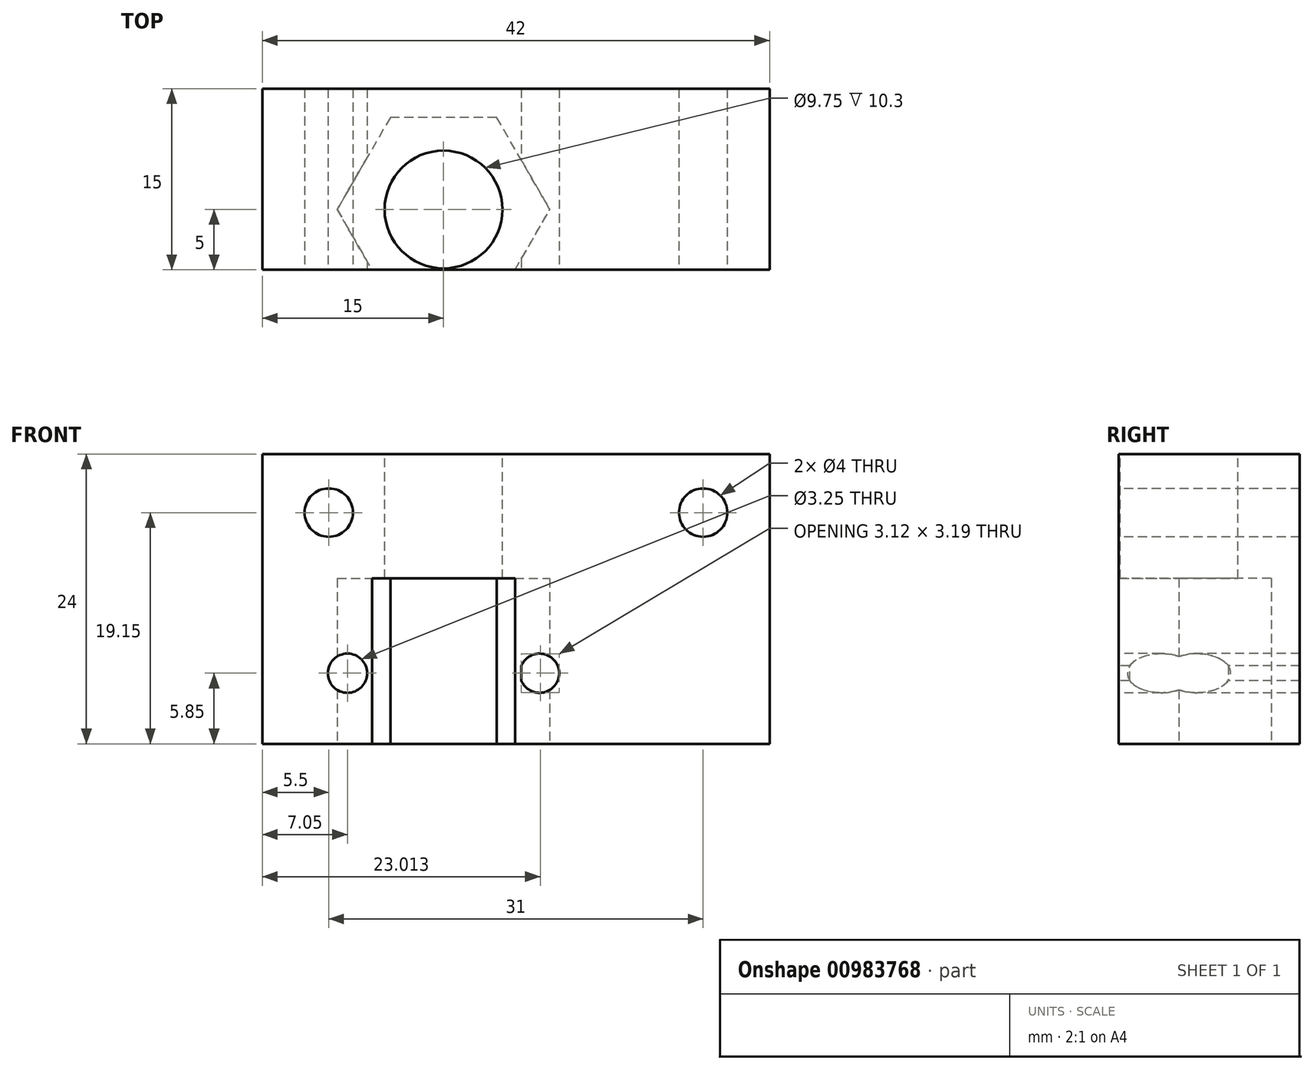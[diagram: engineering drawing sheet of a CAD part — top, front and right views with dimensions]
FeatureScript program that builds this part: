
annotation { "Feature Type Name" : "Feature", "Feature Type Description" : "" }
export const myFeature = defineFeature(function(context is Context, id is Id, definition is map)
    precondition{}
    {
        {
            var Q0;
            Q0=qCreatedBy(makeId("Front.planeOp"),FACE);
            var sketch = newSketch(context, id + "F0", { "sketchPlane" : qUnion([Q0])});
            skLineSegment(sketch, "E0.bottom", {"start": v(0, 0) * mm, "end": v(42, 0) * mm});
            skLineSegment(sketch, "E0.top", {"start": v(0, 24) * mm, "end": v(42, 24) * mm});
            skLineSegment(sketch, "E0.left", {"start": v(0, 0) * mm, "end": v(0, 24) * mm});
            skLineSegment(sketch, "E0.right", {"start": v(42, 0) * mm, "end": v(42, 24) * mm});
            skSolve(sketch);
        }
        {
            var Q0;
            Q0=makeQuery(id+"F0.imprint","IMPRINT",FACE,{"disambiguationData":[TD([[makeQuery(id+"F0.imprint","IMPRINT",EDGE,{"derivedFrom":sQuery(id+"F0.wireOp",EDGE,"E0.bottom")}),1.0]])]});
            extrude(context, id + "F1", {"entities" : qUnion([Q0]), "depth" : 15 * mm, "offsetDistance" : 25 * mm});
        }
        {
            var Q0;
            Q0=makeQuery(id+"F1.opExtrude","CAP_FACE",FACE,{"disambiguationData":[OSD([sQuery(id+"F0.wireOp",EDGE,"E0.bottom"),sQuery(id+"F0.wireOp",EDGE,"E0.top"),sQuery(id+"F0.wireOp",EDGE,"E0.left"),sQuery(id+"F0.wireOp",EDGE,"E0.right")])],"isStart":false});
            var sketch = newSketch(context, id + "F2", { "sketchPlane" : qUnion([Q0])});
            skCircle(sketch, "E1", {"center": v(5.5, 19.15) * mm, "radius": 2 * mm});
            skCircle(sketch, "E2", {"center": v(36.5, 19.15) * mm, "radius": 2 * mm});
            skSolve(sketch);
        }
        {
            var Q0;
            Q0=makeQuery(id+"F2.imprint","IMPRINT",FACE,{"disambiguationData":[TD([[makeQuery(id+"F2.imprint","IMPRINT",EDGE,{"derivedFrom":sQuery(id+"F2.wireOp",EDGE,"E1")}),1.0]])]});
            var Q1;
            Q1=makeQuery(id+"F2.imprint","IMPRINT",FACE,{"disambiguationData":[TD([[makeQuery(id+"F2.imprint","IMPRINT",EDGE,{"derivedFrom":sQuery(id+"F2.wireOp",EDGE,"E2")}),1.0]])]});
            extrude(context, id + "F3", {"entities" : qUnion([Q0, Q1]), "operationType" : NewBodyOperationType.REMOVE, "oppositeDirection" : true, "depth" : 25 * mm, "offsetDistance" : 25 * mm});
        }
        {
            var Q0;
            Q0=makeQuery(id+"F1.opExtrude","SWEPT_FACE",FACE,{"disambiguationData":[OSD([sQuery(id+"F0.wireOp",EDGE,"E0.top")])]});
            var sketch = newSketch(context, id + "F4", { "sketchPlane" : qUnion([Q0])});
            skCircle(sketch, "E3", {"center": v(15, -10) * mm, "radius": 4.88 * mm});
            skSolve(sketch);
        }
        {
            var Q0;
            Q0=makeQuery(id+"F4.imprint","IMPRINT",FACE,{"disambiguationData":[TD([[makeQuery(id+"F4.imprint","IMPRINT",EDGE,{"derivedFrom":sQuery(id+"F4.wireOp",EDGE,"E3")}),1.0]])]});
            extrude(context, id + "F5", {"entities" : qUnion([Q0]), "operationType" : NewBodyOperationType.REMOVE, "oppositeDirection" : true, "depth" : 10.3 * mm, "offsetDistance" : 25 * mm});
        }
        {
            var Q0;
            Q0=makeQuery(id+"F1.opExtrude","SWEPT_FACE",FACE,{"disambiguationData":[OSD([sQuery(id+"F0.wireOp",EDGE,"E0.bottom")])]});
            var sketch = newSketch(context, id + "F6", { "sketchPlane" : qUnion([Q0])});
            skCircle(sketch, "E4.0", {"center": v(15, 10) * mm, "radius": 4.88 * mm});
            skCircle(sketch, "E5.cCircle", {"center": v(15, 10) * mm, "radius": 7.63 * mm, "construction": true});
            skLineSegment(sketch, "E5.0", {"start": v(10.6, 17.62) * mm, "end": v(19.4, 17.62) * mm});
            skLineSegment(sketch, "E5.1", {"start": v(19.4, 17.63) * mm, "end": v(23.8, 10) * mm});
            skLineSegment(sketch, "E5.2", {"start": v(23.8, 10) * mm, "end": v(19.4, 2.37) * mm});
            skLineSegment(sketch, "E5.3", {"start": v(19.4, 2.38) * mm, "end": v(10.6, 2.38) * mm});
            skLineSegment(sketch, "E5.4", {"start": v(10.6, 2.37) * mm, "end": v(6.2, 10) * mm});
            skLineSegment(sketch, "E5.5", {"start": v(6.2, 10) * mm, "end": v(10.6, 17.63) * mm});
            skPoint(sketch, "E5.0.midPoint", {"position": v(15, 17.62) * mm});
            skSolve(sketch);
        }
        {
            var Q0;
            Q0=makeQuery(id+"F6.imprint","IMPRINT",FACE,{"disambiguationData":[TD([[makeQuery(id+"F6.imprint","IMPRINT",EDGE,{"derivedFrom":sQuery(id+"F6.wireOp",EDGE,"E4.0")}),1.0]])]});
            var Q1;
            Q1=makeQuery(id+"F6.imprint","IMPRINT",FACE,{"disambiguationData":[TD([[makeQuery(id+"F6.imprint","IMPRINT",EDGE,{"derivedFrom":sQuery(id+"F6.wireOp",EDGE,"E4.0")}),-1.0]])]});
            var Q2;
            Q2=makeQuery(id+"F5.boolean.opBoolean","COPY",FACE,{"derivedFrom":makeQuery(id+"F5.opExtrude","CAP_FACE",FACE,{"disambiguationData":[OSD([sQuery(id+"F4.wireOp",EDGE,"E3")])],"isStart":false})});
            extrude(context, id + "F7", {"entities" : qUnion([Q0, Q1]), "operationType" : NewBodyOperationType.REMOVE, "endBound" : BoundingType.UP_TO_SURFACE, "oppositeDirection" : true, "depth" : 25 * mm, "endBoundEntityFace" : qUnion([Q2]), "offsetDistance" : 25 * mm});
        }
        {
            var Q0;
            Q0=makeQuery(id+"F1.opExtrude","CAP_FACE",FACE,{"disambiguationData":[OSD([sQuery(id+"F0.wireOp",EDGE,"E0.bottom"),sQuery(id+"F0.wireOp",EDGE,"E0.top"),sQuery(id+"F0.wireOp",EDGE,"E0.left"),sQuery(id+"F0.wireOp",EDGE,"E0.right")])],"isStart":false});
            var sketch = newSketch(context, id + "F8", { "sketchPlane" : qUnion([Q0])});
            skLineSegment(sketch, "E6.0", {"start": v(23.8, 13.7) * mm, "end": v(23.8, 0) * mm});
            skLineSegment(sketch, "E7.0", {"start": v(6.2, 13.7) * mm, "end": v(6.2, 0) * mm});
            skLineSegment(sketch, "E8.0", {"start": v(10.6, 13.7) * mm, "end": v(19.4, 13.7) * mm});
            skCircle(sketch, "E9", {"center": v(7.05, 5.85) * mm, "radius": 1.63 * mm});
            skCircle(sketch, "E10", {"center": v(22.95, 5.85) * mm, "radius": 1.63 * mm});
            skLineSegment(sketch, "E11", {"start": v(6.2, 7.35) * mm, "end": v(23.8, 7.35) * mm});
            skLineSegment(sketch, "E12", {"start": v(8.55, 0) * mm, "end": v(8.55, 7.35) * mm});
            skLineSegment(sketch, "E13", {"start": v(21.45, 7.35) * mm, "end": v(21.45, 0) * mm});
            skSolve(sketch);
        }
        {
            var Q0;
            {var subQ0=sQuery(id+"F8.wireOp",EDGE,"E9");var subQ1=sQuery(id+"F8.wireOp",EDGE,"E7.0");var subQ2=makeQuery(id+"F8.imprint","INTERSECT",VERTEX,{"disambiguationData":[OD(0.0)],"derivedFrom":[subQ1,subQ0]});Q0=makeQuery(id+"F8.imprint","IMPRINT",FACE,{"disambiguationData":[TD([[makeQuery(id+"F8.imprint","IMPRINT",EDGE,{"disambiguationData":[TD([[subQ2,-1.0]])],"derivedFrom":subQ1}),-1.0]])]});}
            var Q1;
            {var subQ0=sQuery(id+"F8.wireOp",EDGE,"E9");var subQ1=sQuery(id+"F8.wireOp",EDGE,"E7.0");var subQ5=makeQuery(id+"F8.imprint","INTERSECT",VERTEX,{"disambiguationData":[OD(0.0)],"derivedFrom":[subQ1,subQ0]});Q1=makeQuery(id+"F8.imprint","IMPRINT",FACE,{"disambiguationData":[TD([[makeQuery(id+"F8.imprint","IMPRINT",EDGE,{"disambiguationData":[TD([[subQ5,-1.0]])],"derivedFrom":subQ1}),1.0]])]});}
            var Q2;
            {var subQ0=sQuery(id+"F8.wireOp",EDGE,"E11");var subQ1=sQuery(id+"F8.wireOp",EDGE,"E9");var subQ2=makeQuery(id+"F8.imprint","INTERSECT",VERTEX,{"disambiguationData":[OD(0.0)],"derivedFrom":[subQ1,subQ0]});Q2=makeQuery(id+"F8.imprint","IMPRINT",FACE,{"disambiguationData":[TD([[makeQuery(id+"F8.imprint","IMPRINT",EDGE,{"disambiguationData":[TD([[subQ2,-1.0]])],"derivedFrom":subQ1}),1.0]])]});}
            var Q3;
            {var subQ0=sQuery(id+"F8.wireOp",EDGE,"E12");var subQ1=sQuery(id+"F8.wireOp",EDGE,"E9");var subQ2=makeQuery(id+"F8.imprint","INTERSECT",VERTEX,{"disambiguationData":[OD(0.0)],"derivedFrom":[subQ1,subQ0]});Q3=makeQuery(id+"F8.imprint","IMPRINT",FACE,{"disambiguationData":[TD([[makeQuery(id+"F8.imprint","IMPRINT",EDGE,{"disambiguationData":[TD([[subQ2,1.0]])],"derivedFrom":subQ1}),1.0]])]});}
            var Q4;
            {var subQ0=sQuery(id+"F8.wireOp",EDGE,"E13");var subQ1=sQuery(id+"F8.wireOp",EDGE,"E10");var subQ2=makeQuery(id+"F8.imprint","INTERSECT",VERTEX,{"disambiguationData":[OD(0.0)],"derivedFrom":[subQ1,subQ0]});Q4=makeQuery(id+"F8.imprint","IMPRINT",FACE,{"disambiguationData":[TD([[makeQuery(id+"F8.imprint","IMPRINT",EDGE,{"disambiguationData":[TD([[subQ2,-1.0]])],"derivedFrom":subQ1}),1.0]])]});}
            var Q5;
            {var subQ0=sQuery(id+"F8.wireOp",EDGE,"E11");var subQ1=sQuery(id+"F8.wireOp",EDGE,"E10");var subQ2=makeQuery(id+"F8.imprint","INTERSECT",VERTEX,{"disambiguationData":[OD(0.0)],"derivedFrom":[subQ1,subQ0]});Q5=makeQuery(id+"F8.imprint","IMPRINT",FACE,{"disambiguationData":[TD([[makeQuery(id+"F8.imprint","IMPRINT",EDGE,{"disambiguationData":[TD([[subQ2,-1.0]])],"derivedFrom":subQ1}),1.0]])]});}
            var Q6;
            {var subQ0=sQuery(id+"F8.wireOp",EDGE,"E10");var subQ1=sQuery(id+"F8.wireOp",EDGE,"E6.0");var subQ2=makeQuery(id+"F8.imprint","INTERSECT",VERTEX,{"disambiguationData":[OD(0.0)],"derivedFrom":[subQ1,subQ0]});Q6=makeQuery(id+"F8.imprint","IMPRINT",FACE,{"disambiguationData":[TD([[makeQuery(id+"F8.imprint","IMPRINT",EDGE,{"disambiguationData":[TD([[subQ2,-1.0]])],"derivedFrom":subQ1}),1.0]])]});}
            var Q7;
            {var subQ1=sQuery(id+"F8.wireOp",EDGE,"E10");var subQ5=sQuery(id+"F8.wireOp",EDGE,"E6.0");var subQ6=makeQuery(id+"F8.imprint","INTERSECT",VERTEX,{"disambiguationData":[OD(0.0)],"derivedFrom":[subQ5,subQ1]});Q7=makeQuery(id+"F8.imprint","IMPRINT",FACE,{"disambiguationData":[TD([[makeQuery(id+"F8.imprint","IMPRINT",EDGE,{"disambiguationData":[TD([[subQ6,-1.0]])],"derivedFrom":subQ5}),-1.0]])]});}
            extrude(context, id + "F9", {"entities" : qUnion([Q0, Q1, Q2, Q3, Q4, Q5, Q6, Q7]), "operationType" : NewBodyOperationType.REMOVE, "oppositeDirection" : true, "depth" : 25 * mm, "offsetDistance" : 25 * mm});
        }
    });
